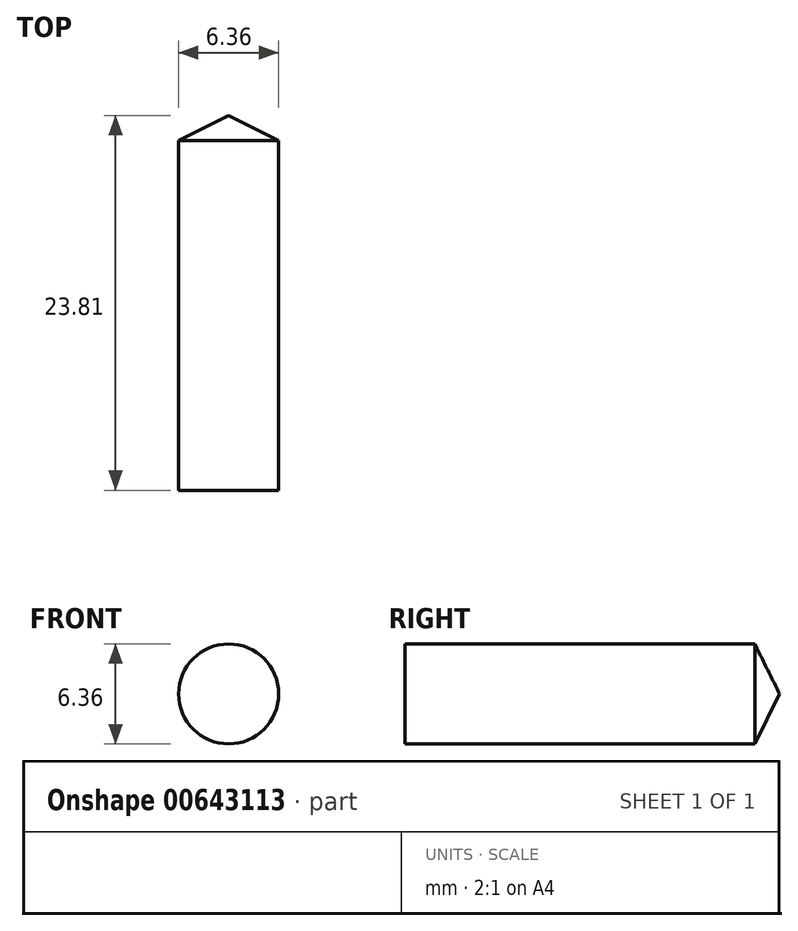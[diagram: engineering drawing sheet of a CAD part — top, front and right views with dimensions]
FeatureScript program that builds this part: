
annotation { "Feature Type Name" : "Feature", "Feature Type Description" : "" }
export const myFeature = defineFeature(function(context is Context, id is Id, definition is map)
    precondition{}
    {
        {
            var Q0;
            Q0=qCreatedBy(makeId("Front.planeOp"),FACE);
            var sketch = newSketch(context, id + "F0", { "sketchPlane" : qUnion([Q0])});
            skCircle(sketch, "E0", {"center": v(0, 0) * mm, "radius": 3.18 * mm});
            skSolve(sketch);
        }
        {
            var Q0;
            Q0 = qSketchRegion(id + "F0", true);
            extrude(context, id + "F1", {"entities" : qUnion([Q0]), "depth" : 22.22 * mm, "offsetDistance" : 25.4 * mm});
        }
        {
            var Q0;
            Q0 = qSketchRegion(id + "F0", true);
            extrude(context, id + "F2", {"entities" : qUnion([Q0]), "operationType" : NewBodyOperationType.ADD, "oppositeDirection" : true, "depth" : 1.59 * mm, "offsetDistance" : 25.4 * mm, "hasDraft" : true, "draftAngle" : 63.5 * degree, "draftPullDirection" : true});
        }
    });
